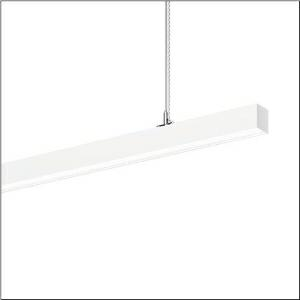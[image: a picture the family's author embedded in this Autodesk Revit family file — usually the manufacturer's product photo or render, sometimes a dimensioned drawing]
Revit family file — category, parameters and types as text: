
# Revit family: silica_r__21_51mx33tbt9w_4d61
name_source: partatom
category: Lighting Fixtures
units: mm (PartAtom-declared; Revit-internal decimal feet)

## family parameters
Cut with Voids When Loaded = No
Host = Face
Light Source = No
Part Type = Normal
Room Calculation Point = No
Round Connector Dimension = Use Diameter
Shared = No

## types (1)
- --- (1 x LED, 7170 lm, 67.4 W, 6500K)
    Apparent Load = 67 VA
    CIE Flux Codes = 78 96 99 56 100
    Color Rendering = 80
    Color Temperature = 6500K
    Default Elevation = 1800 mm
    Description = Silica® 21, office luminaire, primary optical cover: prismatic diffuser, of PMMA, CAT 2 (L<= 3000cd/m²), light emission: direct/indirect distribution, primary light characteristic: symmetric, installation type: suspended mounting, LED, rated luminous flux: 7.170lm, luminous efficacy: 101lm/W, light colour: 8tw, colour temperature: 2700..6500K, control gear: ECG DALI, with terminal, 3+2-pole, max. 2.5mm², mains connection: 220..240V, AC, 50/60Hz, rated input power: 70.8W, luminaire housing, of aluminium, traffic white (RAL 9016), length: 1.504mm, width: 53mm, height: 53mm, protection rating (complete): IP20, insulation class (complete): insulation class I (protective earthing), certification: CE, permissible operating ambient temperature: 0..+35°C, standard: EN 50419, packaging unit: 1 piece
    Height = 53 mm
    Lamp = 1 x LED
    Lamp Light Flux = 7170 lm
    Lamp Power = 67.4 W
    Lamp count = 1
    Length = 1504 mm
    Luminous efficacy = 106 lm/W
    Manufacturer = Siteco
    ModVariant = No
    Model = 51MX33TBT9W
    Mounting Place = Ceiling
    Mounting Type = Pendant
    Number of Poles = 1
    OnlyDefault = Yes
    Power Factor = 1
    Product Name = Silica® 21
    Product group = office luminaire | ceiling pendant
    ProductGroupID = 905
    Protection Class = Protection class I
    Protection Degree = IP 20
    RLX_Detail_Level = 1
    RlxData = <blob elided: 18229 chars, md5=7068b5d3>
    Socket = socket
    Standby Power = 0 W
    System Light Flux = 7170 lm
    System Power = 67 W
    Type Comments = individual setting
    Type Image = l_1251642.jpg
    URL = http://relux.com
    VarID = @adj_045867
    Voltage = 0 V
    Weight = 0.00 kg
    Width = 53 mm

## geometry (parser evidence)
native form markers: Blend x4, Sweep x12
no freeform markers — native parametric forms only
